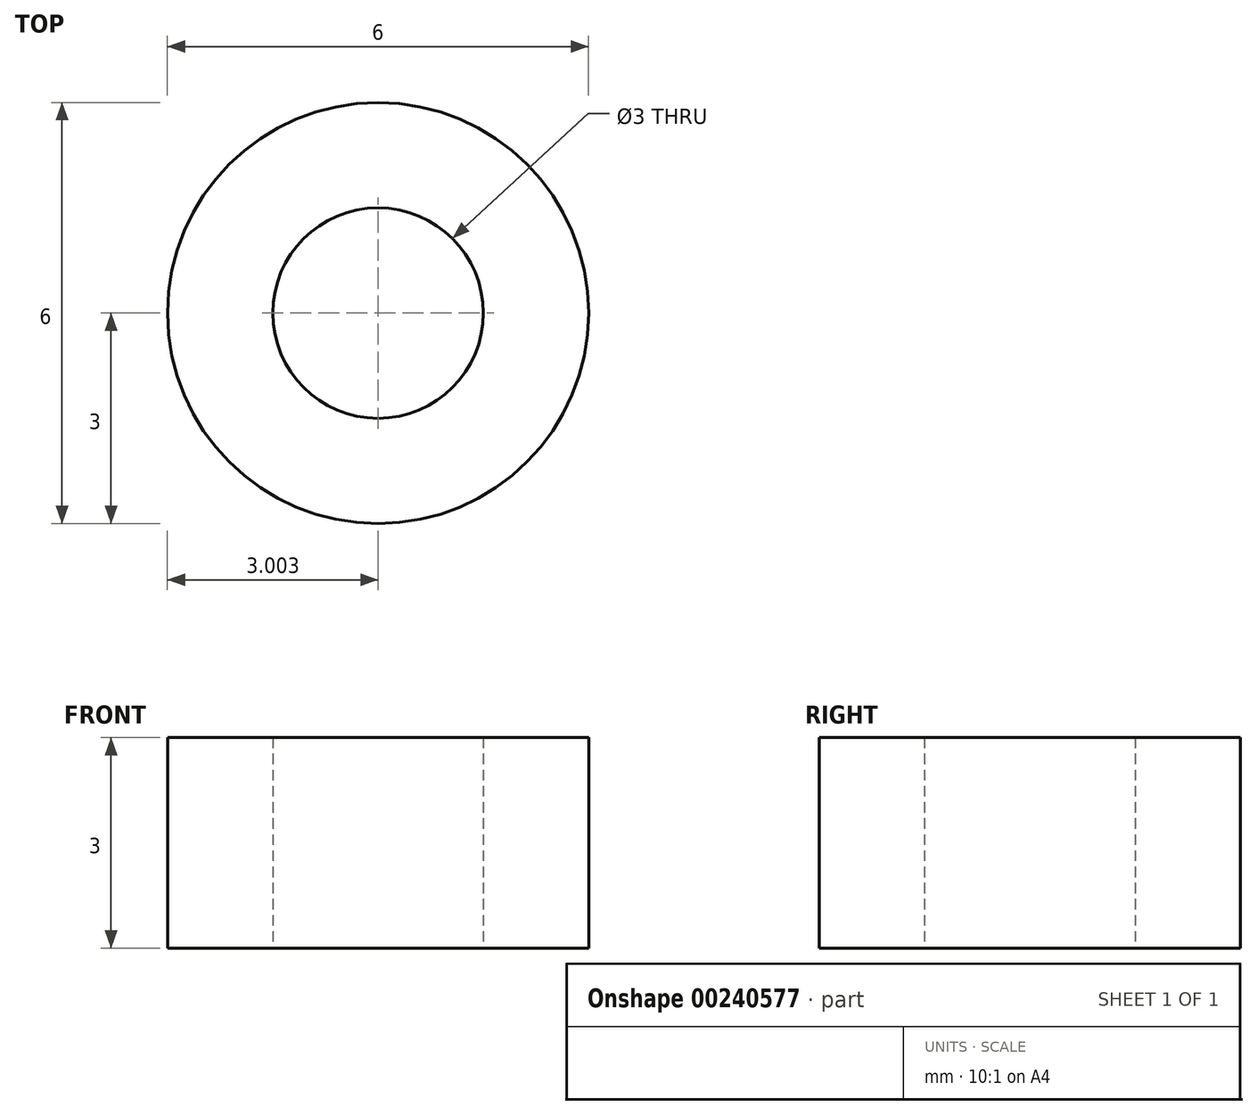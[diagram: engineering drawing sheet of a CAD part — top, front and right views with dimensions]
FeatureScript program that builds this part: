
annotation { "Feature Type Name" : "Feature", "Feature Type Description" : "" }
export const myFeature = defineFeature(function(context is Context, id is Id, definition is map)
    precondition{}
    {
        {
            var Q0;
            Q0=qCreatedBy(makeId("Top.planeOp"),FACE);
            var sketch = newSketch(context, id + "F0", { "sketchPlane" : qUnion([Q0])});
            skCircle(sketch, "E0", {"center": v(-0.48, 0) * mm, "radius": 3 * mm});
            skCircle(sketch, "E1", {"center": v(-0.48, 0) * mm, "radius": 1.5 * mm});
            skSolve(sketch);
        }
        {
            var Q0;
            Q0=makeQuery(id+"F0.imprint","IMPRINT",FACE,{"disambiguationData":[TD([[makeQuery(id+"F0.imprint","IMPRINT",EDGE,{"derivedFrom":sQuery(id+"F0.wireOp",EDGE,"E0")}),1.0]])]});
            extrude(context, id + "F1", {"entities" : qUnion([Q0]), "depth" : 3 * mm});
        }
    });
